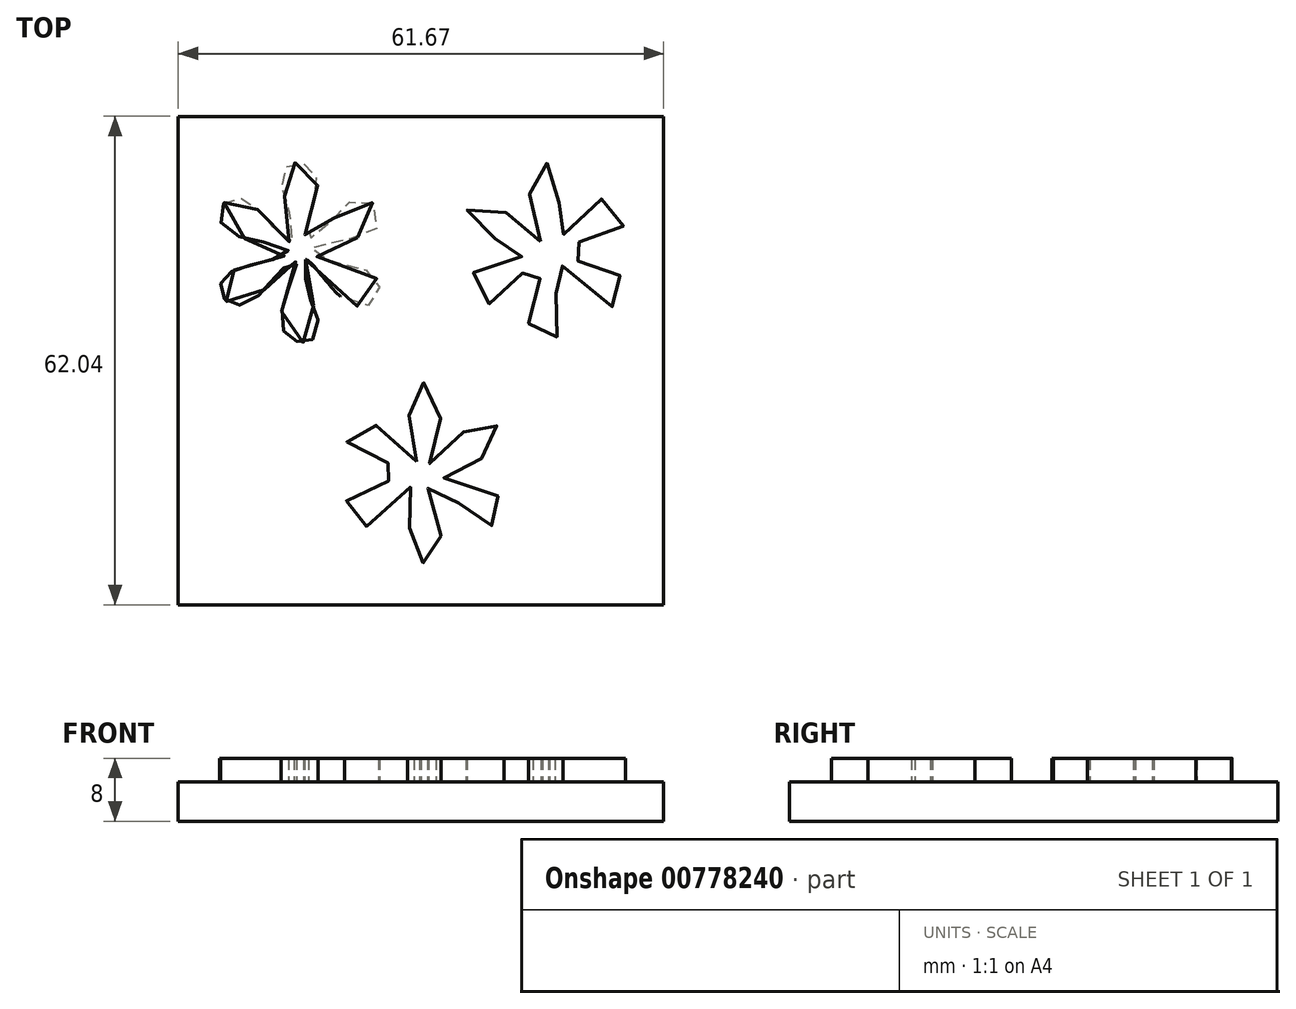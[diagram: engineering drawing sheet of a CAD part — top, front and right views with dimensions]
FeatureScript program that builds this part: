
annotation { "Feature Type Name" : "Feature", "Feature Type Description" : "" }
export const myFeature = defineFeature(function(context is Context, id is Id, definition is map)
    precondition{}
    {
        {
            var Q0;
            Q0=qCreatedBy(makeId("Top.planeOp"),FACE);
            var sketch = newSketch(context, id + "F0", { "sketchPlane" : qUnion([Q0])});
            skLineSegment(sketch, "E0.bottom", {"start": v(0, 62.04) * mm, "end": v(61.67, 62.04) * mm});
            skLineSegment(sketch, "E0.top", {"start": v(0, 0) * mm, "end": v(61.67, 0) * mm});
            skLineSegment(sketch, "E0.left", {"start": v(0, 62.04) * mm, "end": v(0, 0) * mm});
            skLineSegment(sketch, "E0.right", {"start": v(61.67, 62.04) * mm, "end": v(61.67, 0) * mm});
            skSolve(sketch);
        }
        {
            var Q0;
            Q0 = qSketchRegion(id + "F0", true);
            extrude(context, id + "F1", {"entities" : qUnion([Q0]), "depth" : 5 * mm, "offsetDistance" : 25 * mm});
        }
        {
            var Q0;
            Q0=makeQuery(id+"F1.opExtrude","CAP_FACE",FACE,{"disambiguationData":[OSD([sQuery(id+"F0.wireOp",EDGE,"E0.bottom"),sQuery(id+"F0.wireOp",EDGE,"E0.top"),sQuery(id+"F0.wireOp",EDGE,"E0.left"),sQuery(id+"F0.wireOp",EDGE,"E0.right")])],"isStart":false});
            var sketch = newSketch(context, id + "F2", { "sketchPlane" : qUnion([Q0])});
            skFitSpline(sketch, "E1", {"points": [v(30.26, 18.18) * mm, v(30.63, 19.91) * mm, v(29.52, 23.5) * mm, v(29.09, 26.72) * mm, v(30.26, 28.02) * mm, v(31.87, 28.02) * mm, v(33.17, 26.16) * mm, v(33.3, 23.31) * mm, v(32.24, 20.65) * mm, v(31.93, 17.93) * mm, v(33.6, 19.23) * mm, v(35.95, 21.58) * mm, v(37.69, 23.25) * mm, v(39.42, 23.44) * mm, v(40.78, 22.26) * mm, v(41.27, 20.1) * mm, v(37.75, 18.36) * mm, v(32.74, 16.94) * mm, v(35.77, 15.46) * mm, v(39.85, 14.34) * mm, v(41.21, 12.98) * mm, v(41.27, 11.37) * mm, v(40.1, 10.14) * mm, v(38.43, 10.14) * mm, v(36.57, 11.74) * mm, v(34.53, 14.1) * mm, v(31.8, 15.89) * mm, v(32.06, 13.54) * mm, v(32.98, 10.5) * mm, v(33.42, 8.1) * mm, v(32.98, 6.24) * mm, v(31.75, 5.3) * mm, v(30.14, 5.8) * mm, v(29.2, 7.41) * mm, v(29.7, 10.75) * mm, v(30.7, 15.4) * mm, v(27.6, 13.17) * mm, v(24.75, 10.2) * mm, v(21.97, 10.38) * mm, v(21.17, 12.05) * mm, v(21.48, 13.35) * mm, v(23.7, 14.84) * mm, v(26.67, 15.7) * mm, v(29.95, 16.82) * mm, v(25.56, 18.24) * mm, v(22.9, 19.23) * mm, v(21.41, 20.72) * mm, v(21.66, 22.94) * mm, v(24.63, 23.07) * mm, v(27.54, 20.22) * mm, v(30.26, 18.18) * mm]});
            skFitSpline(sketch, "E2", {"points": [v(16.22, 43.86) * mm, v(16.15, 41.94) * mm, v(16.71, 39.03) * mm, v(17.7, 36.5) * mm, v(17.27, 33.9) * mm, v(15.9, 33.34) * mm, v(14.42, 33.7) * mm, v(13.25, 35.2) * mm, v(13.3, 38.04) * mm, v(14.36, 41.07) * mm, v(14.92, 43.6) * mm, v(13, 42.43) * mm, v(11.51, 40.76) * mm, v(10.52, 39.59) * mm, v(8.36, 38.16) * mm, v(6.44, 38.29) * mm, v(5.57, 39.46) * mm, v(5.45, 41) * mm, v(6.5, 42.19) * mm, v(8.8, 43.05) * mm, v(11.27, 43.67) * mm, v(14.05, 44.78) * mm, v(11.33, 45.96) * mm, v(7.55, 46.83) * mm, v(5.33, 48.8) * mm, v(5.76, 50.97) * mm, v(6.75, 51.65) * mm, v(8.73, 51.4) * mm, v(10.03, 50.3) * mm, v(11.08, 49.3) * mm, v(12.13, 47.88) * mm, v(14.48, 46.08) * mm, v(14.38, 48.98) * mm, v(13.5, 51.9) * mm, v(13.1, 54.24) * mm, v(13.8, 55.64) * mm, v(14.96, 56.17) * mm, v(16.13, 56) * mm, v(17, 55.3) * mm, v(17.7, 53.54) * mm, v(17.18, 51.09) * mm, v(16.54, 48.22) * mm, v(16.01, 46.24) * mm, v(18.06, 47.47) * mm, v(19.81, 49.16) * mm, v(21.39, 50.91) * mm, v(23.78, 51.55) * mm, v(25.36, 49.92) * mm, v(24.9, 47.35) * mm, v(21.62, 46.47) * mm, v(16.6, 45.01) * mm, v(18.88, 43.84) * mm, v(24.3, 42.27) * mm, v(25.47, 40.87) * mm, v(25.42, 39.23) * mm, v(23.66, 37.89) * mm, v(20.16, 39.58) * mm, v(16.22, 43.86) * mm]});
            skFitSpline(sketch, "E3", {"points": [v(46.03, 46.1) * mm, v(45.88, 48.06) * mm, v(44.86, 51.4) * mm, v(44.43, 54.49) * mm, v(45.56, 55.93) * mm, v(47.28, 55.97) * mm, v(48.68, 54.56) * mm, v(48.53, 51.52) * mm, v(47.12, 46.42) * mm, v(48.4, 46.65) * mm, v(50.7, 48.76) * mm, v(53.05, 51.33) * mm, v(55.43, 51.33) * mm, v(56.63, 50) * mm, v(56.32, 47.78) * mm, v(53.55, 46.5) * mm, v(51.25, 46.1) * mm, v(47.9, 45.13) * mm, v(50.05, 43.86) * mm, v(53.32, 43.14) * mm, v(55.54, 42.36) * mm, v(56.36, 41.43) * mm, v(56.83, 39.83) * mm, v(55.82, 38.2) * mm, v(53.98, 38) * mm, v(49.46, 42.36) * mm, v(47.36, 43.86) * mm, v(47.44, 41.47) * mm, v(48.68, 37.18) * mm, v(48.8, 35.2) * mm, v(47.94, 33.87) * mm, v(46.58, 33.52) * mm, v(44.94, 34.5) * mm, v(44.55, 36.52) * mm, v(45.14, 38.62) * mm, v(46, 41.55) * mm, v(46.11, 43.86) * mm, v(44.43, 42.83) * mm, v(43.1, 41.43) * mm, v(41.4, 39.44) * mm, v(39.06, 38.16) * mm, v(36.87, 39.56) * mm, v(37.3, 42.01) * mm, v(39.13, 42.91) * mm, v(41.43, 43.86) * mm, v(45.1, 44.78) * mm, v(40.65, 46.5) * mm, v(39.95, 46.57) * mm, v(37.18, 48.06) * mm, v(36.68, 50.08) * mm, v(38, 51.52) * mm, v(40.73, 50.63) * mm, v(43.3, 48.06) * mm, v(45.56, 46.22) * mm, v(46.03, 46.1) * mm]});
            skSolve(sketch);
        }
        {
            var Q0;
            Q0=makeQuery(id+"F2.imprint","IMPRINT",FACE,{"disambiguationData":[TD([[makeQuery(id+"F2.imprint","IMPRINT",EDGE,{"derivedFrom":sQuery(id+"F2.wireOp",EDGE,"E1")}),-1.0]])]});
            var Q1;
            Q1=makeQuery(id+"F2.imprint","IMPRINT",FACE,{"disambiguationData":[TD([[makeQuery(id+"F2.imprint","IMPRINT",EDGE,{"derivedFrom":sQuery(id+"F2.wireOp",EDGE,"E2")}),-1.0]])]});
            var Q2;
            Q2=makeQuery(id+"F2.imprint","IMPRINT",FACE,{"disambiguationData":[TD([[makeQuery(id+"F2.imprint","IMPRINT",EDGE,{"derivedFrom":sQuery(id+"F2.wireOp",EDGE,"E3")}),-1.0]])]});
            extrude(context, id + "F3", {"entities" : qUnion([Q0, Q1, Q2]), "operationType" : NewBodyOperationType.ADD, "depth" : 3 * mm, "offsetDistance" : 25 * mm});
        }
    });
